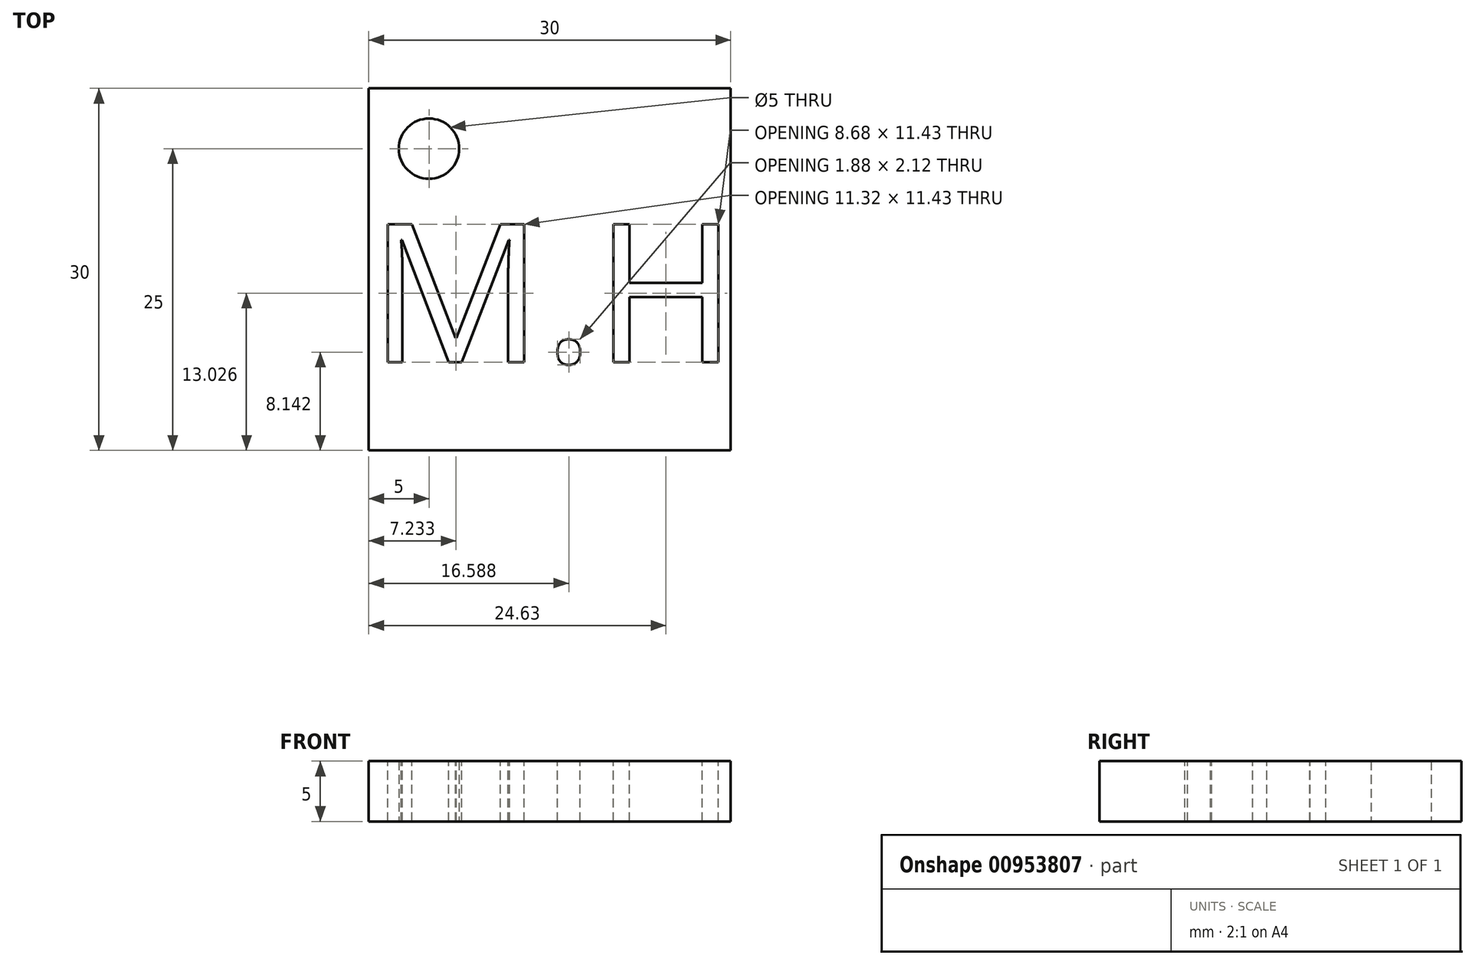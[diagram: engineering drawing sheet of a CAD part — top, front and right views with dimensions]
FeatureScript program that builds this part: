
annotation { "Feature Type Name" : "Feature", "Feature Type Description" : "" }
export const myFeature = defineFeature(function(context is Context, id is Id, definition is map)
    precondition{}
    {
        {
            var Q0;
            Q0=qCreatedBy(makeId("Top.planeOp"),FACE);
            var sketch = newSketch(context, id + "F0", { "sketchPlane" : qUnion([Q0])});
            skLineSegment(sketch, "E0.bottom", {"start": v(0, 0) * mm, "end": v(30, 0) * mm});
            skLineSegment(sketch, "E0.top", {"start": v(0, 30) * mm, "end": v(30, 30) * mm});
            skLineSegment(sketch, "E0.left", {"start": v(0, 0) * mm, "end": v(0, 30) * mm});
            skLineSegment(sketch, "E0.right", {"start": v(30, 0) * mm, "end": v(30, 30) * mm});
            skCircle(sketch, "E1", {"center": v(5, 25) * mm, "radius": 2.5 * mm});
            skSolve(sketch);
        }
        {
            var Q0;
            Q0=makeQuery(id+"F0.imprint","IMPRINT",FACE,{"disambiguationData":[TD([[makeQuery(id+"F0.imprint","IMPRINT",EDGE,{"derivedFrom":sQuery(id+"F0.wireOp",EDGE,"E0.bottom")}),1.0]])]});
            extrude(context, id + "F1", {"entities" : qUnion([Q0]), "depth" : 5 * mm, "offsetDistance" : 25 * mm});
        }
        {
            var Q0;
            Q0=makeQuery(id+"F1.opExtrude","CAP_FACE",FACE,{"disambiguationData":[OSD([sQuery(id+"F0.wireOp",EDGE,"E0.bottom"),sQuery(id+"F0.wireOp",EDGE,"E0.top"),sQuery(id+"F0.wireOp",EDGE,"E0.left"),sQuery(id+"F0.wireOp",EDGE,"E0.right"),sQuery(id+"F0.wireOp",EDGE,"E1")])],"isStart":false});
            var sketch = newSketch(context, id + "F2", { "sketchPlane" : qUnion([Q0])});
            skText(sketch, "E2", { "text": "M.H", "fontName": "OpenSans-Regular.ttf"});
            const initialGuessF2  = {"E2": [0, 0.00731, 1, 0, 0.01153]};
            skSetInitialGuess(sketch, initialGuessF2);
            skSolve(sketch);
        }
        {
            var Q0;
            Q0 = qSketchRegion(id + "F2", true);
            extrude(context, id + "F3", {"entities" : qUnion([Q0]), "operationType" : NewBodyOperationType.REMOVE, "oppositeDirection" : true, "depth" : 25 * mm, "offsetDistance" : 25 * mm});
        }
    });
